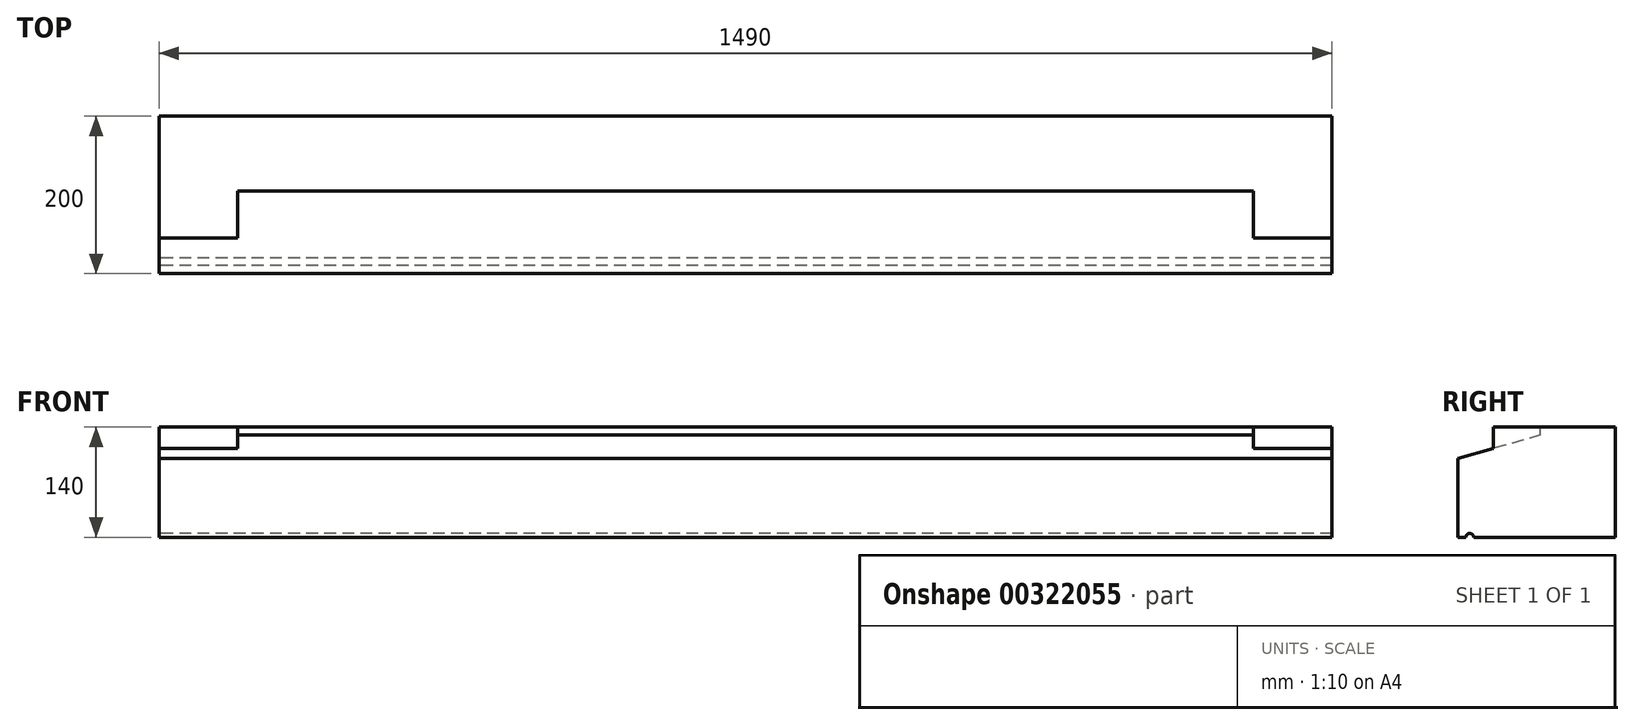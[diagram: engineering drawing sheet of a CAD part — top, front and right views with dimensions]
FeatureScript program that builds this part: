
annotation { "Feature Type Name" : "Feature", "Feature Type Description" : "" }
export const myFeature = defineFeature(function(context is Context, id is Id, definition is map)
    precondition{}
    {
        {
            var Q0;
            Q0=qCreatedBy(makeId("Right.planeOp"),FACE);
            var sketch = newSketch(context, id + "F0", { "sketchPlane" : qUnion([Q0])});
            skLineSegment(sketch, "E0", {"start": v(0, 0) * mm, "end": v(-95, 0) * mm});
            skLineSegment(sketch, "E1", {"start": v(-95, 0) * mm, "end": v(-95, -10) * mm});
            skLineSegment(sketch, "E2", {"start": v(-95, -10) * mm, "end": v(-200, -40) * mm});
            skLineSegment(sketch, "E3", {"start": v(-200, -40) * mm, "end": v(-200, -140) * mm});
            skLineSegment(sketch, "E4", {"start": v(-200, -140) * mm, "end": v(-190, -140) * mm});
            skLineSegment(sketch, "E5", {"start": v(0, -140) * mm, "end": v(0, 0) * mm});
            skArc(sketch, "E6", {"start": v(-180, -140) * mm, "mid": v(-185, -135) * mm, "end": v(-190, -140) * mm});
            skLineSegment(sketch, "E7.trimOffspring", {"start": v(-180, -140) * mm, "end": v(0, -140) * mm});
            skSolve(sketch);
        }
        {
            var Q0;
            Q0=makeQuery(id+"F0.imprint","IMPRINT",FACE,{"disambiguationData":[TD([[makeQuery(id+"F0.imprint","IMPRINT",EDGE,{"derivedFrom":sQuery(id+"F0.wireOp",EDGE,"E0")}),1.0]])]});
            extrude(context, id + "F1", {"entities" : qUnion([Q0]), "endBound" : BoundingType.SYMMETRIC, "depth" : 1490 * mm});
        }
        {
            var Q0;
            Q0=makeQuery(id+"F1.opExtrude","SWEPT_FACE",FACE,{"disambiguationData":[OSD([sQuery(id+"F0.wireOp",EDGE,"E0")])]});
            var sketch = newSketch(context, id + "F2", { "sketchPlane" : qUnion([Q0])});
            skLineSegment(sketch, "E8.bottom", {"start": v(-745, -95) * mm, "end": v(-645, -95) * mm});
            skLineSegment(sketch, "E8.top", {"start": v(-745, -155) * mm, "end": v(-645, -155) * mm});
            skLineSegment(sketch, "E8.left", {"start": v(-745, -95) * mm, "end": v(-745, -155) * mm});
            skLineSegment(sketch, "E8.right", {"start": v(-645, -95) * mm, "end": v(-645, -155) * mm});
            skSolve(sketch);
        }
        {
            var Q0;
            Q0=makeQuery(id+"F2.imprint","IMPRINT",FACE,{"disambiguationData":[TD([[makeQuery(id+"F2.imprint","IMPRINT",EDGE,{"derivedFrom":sQuery(id+"F2.wireOp",EDGE,"E8.bottom")}),1.0]])]});
            var Q1;
            Q1=makeQuery(id+"F1.opExtrude","SWEPT_FACE",FACE,{"disambiguationData":[OSD([sQuery(id+"F0.wireOp",EDGE,"E2")])]});
            extrude(context, id + "F3", {"entities" : qUnion([Q0]), "operationType" : NewBodyOperationType.ADD, "endBound" : BoundingType.UP_TO_SURFACE, "oppositeDirection" : true, "endBoundEntityFace" : qUnion([Q1]), "depth" : 25 * mm});
        }
        {
            var Q0;
            Q0=makeQuery(id+"F3.boolean.opBoolean","MERGE",FACE,{"derivedFrom":[makeQuery(id+"F1.opExtrude","SWEPT_FACE",FACE,{"disambiguationData":[OSD([sQuery(id+"F0.wireOp",EDGE,"E0")])]}),makeQuery(id+"F3.opExtrude","CAP_FACE",FACE,{"disambiguationData":[OSD([sQuery(id+"F2.wireOp",EDGE,"E8.bottom"),sQuery(id+"F2.wireOp",EDGE,"E8.top"),sQuery(id+"F2.wireOp",EDGE,"E8.left"),sQuery(id+"F2.wireOp",EDGE,"E8.right")])],"isStart":true})]});
            var sketch = newSketch(context, id + "F4", { "sketchPlane" : qUnion([Q0])});
            skLineSegment(sketch, "E9.bottom", {"start": v(745, -95) * mm, "end": v(645, -95) * mm});
            skLineSegment(sketch, "E9.top", {"start": v(745, -155) * mm, "end": v(645, -155) * mm});
            skLineSegment(sketch, "E9.left", {"start": v(745, -95) * mm, "end": v(745, -155) * mm});
            skLineSegment(sketch, "E9.right", {"start": v(645, -95) * mm, "end": v(645, -155) * mm});
            skSolve(sketch);
        }
        {
            var Q0;
            Q0=makeQuery(id+"F4.imprint","IMPRINT",FACE,{"disambiguationData":[TD([[makeQuery(id+"F4.imprint","IMPRINT",EDGE,{"derivedFrom":sQuery(id+"F4.wireOp",EDGE,"E9.bottom")}),1.0]])]});
            var Q1;
            Q1=makeQuery(id+"F1.opExtrude","SWEPT_FACE",FACE,{"disambiguationData":[OSD([sQuery(id+"F0.wireOp",EDGE,"E2")])]});
            extrude(context, id + "F5", {"entities" : qUnion([Q0]), "operationType" : NewBodyOperationType.ADD, "endBound" : BoundingType.UP_TO_SURFACE, "oppositeDirection" : true, "endBoundEntityFace" : qUnion([Q1]), "depth" : 25 * mm});
        }
    });
